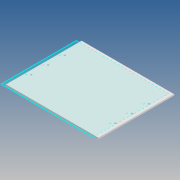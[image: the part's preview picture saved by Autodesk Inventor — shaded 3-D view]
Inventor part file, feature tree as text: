
AUTODESK INVENTOR PART (.ipt)
format: ipt  version: 2020 (Build 240168000, 168)  size: 123,392 bytes
history: native  units: mm
features: reference x18, other x9, extrude x3, sketch x3
ambient origin geometry x8: Origin, YZ Plane, XZ Plane, XY Plane, X Axis, Y Axis, Z Axis, Center Point
bodies: Body1 (feature_tree)
feature tree (33):
  other  "Твердое тело1"
  extrude  "Выдавливание1"  Depth=220.0mm
  extrude  "Выдавливание4"  Depth=180.0mm
  extrude  "Выдавливание5"  Depth=3.0mm TaperAngle=0.0deg
  sketch  "Эскиз1"
  sketch  "Эскиз4"
  reference  "Ссылка1"
  reference  "Ссылка2"
  reference  "Ссылка3"
  reference  "Ссылка4"
  reference  "Ссылка5"
  reference  "Ссылка6"
  sketch  "Эскиз5"
  reference  "Ссылка7"
  reference  "Ссылка8"
  reference  "Ссылка9"
  reference  "Ссылка10"
  reference  "Ссылка11"
  reference  "Ссылка12"
  reference  "Ссылка13"
  reference  "Ссылка14"
  reference  "Ссылка15"
  reference  "Ссылка16"
  reference  "Ссылка17"
  reference  "Ссылка18"
  other  "<path> - Robot.iam"
  other  "000.000 - Robot.iam"
  other  "000.002 - bamper:2"
  other  "000.002 - bamper:1"
  other  "01_Крепление_мотора:2"
  other  "01_Крепление_мотора:4"
  other  "01_Крепление_мотора:3"
  other  "01_Крепление_мотора:1"
note: 1 file-system path scrubbed to <path> (originals preserved in map.json)
